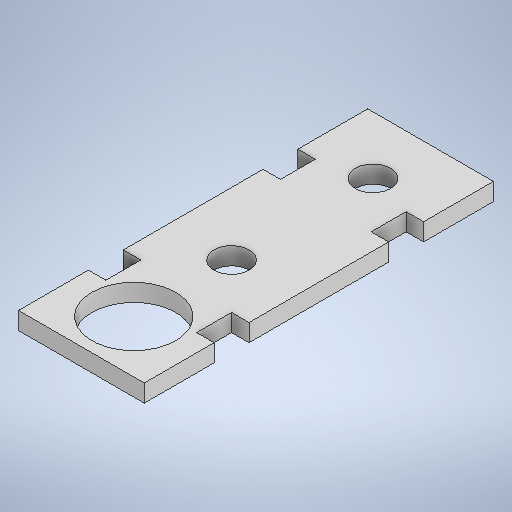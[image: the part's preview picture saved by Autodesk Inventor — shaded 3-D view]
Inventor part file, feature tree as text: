
AUTODESK INVENTOR PART (.ipt)
format: ipt  version: 2025.2 (Build 292293000, 293)  size: 266,240 bytes
history: native  units: mm
features: extrude x1, sketch x1
ambient origin geometry x8: Origin, YZ Plane, XZ Plane, XY Plane, X Axis, Y Axis, Z Axis, Center Point
bodies: Solid1 (feature_tree)
feature tree (2):
  extrude  "Extrusion1"  Depth=100.0mm
  sketch  "Sketch2"  dims[d0=36.0mm d1=100.0mm d2=20.0mm d3=20.0mm d4=10.0mm d5=5.0mm d6=10.0mm d7=5.0mm d8=5.0mm d9=15.0mm d10=24.0mm d13=40.5mm d15=5.0mm d16=0.0mm d17=28.0mm d18=10.1mm d19=40.5mm d20=10.1mm]
